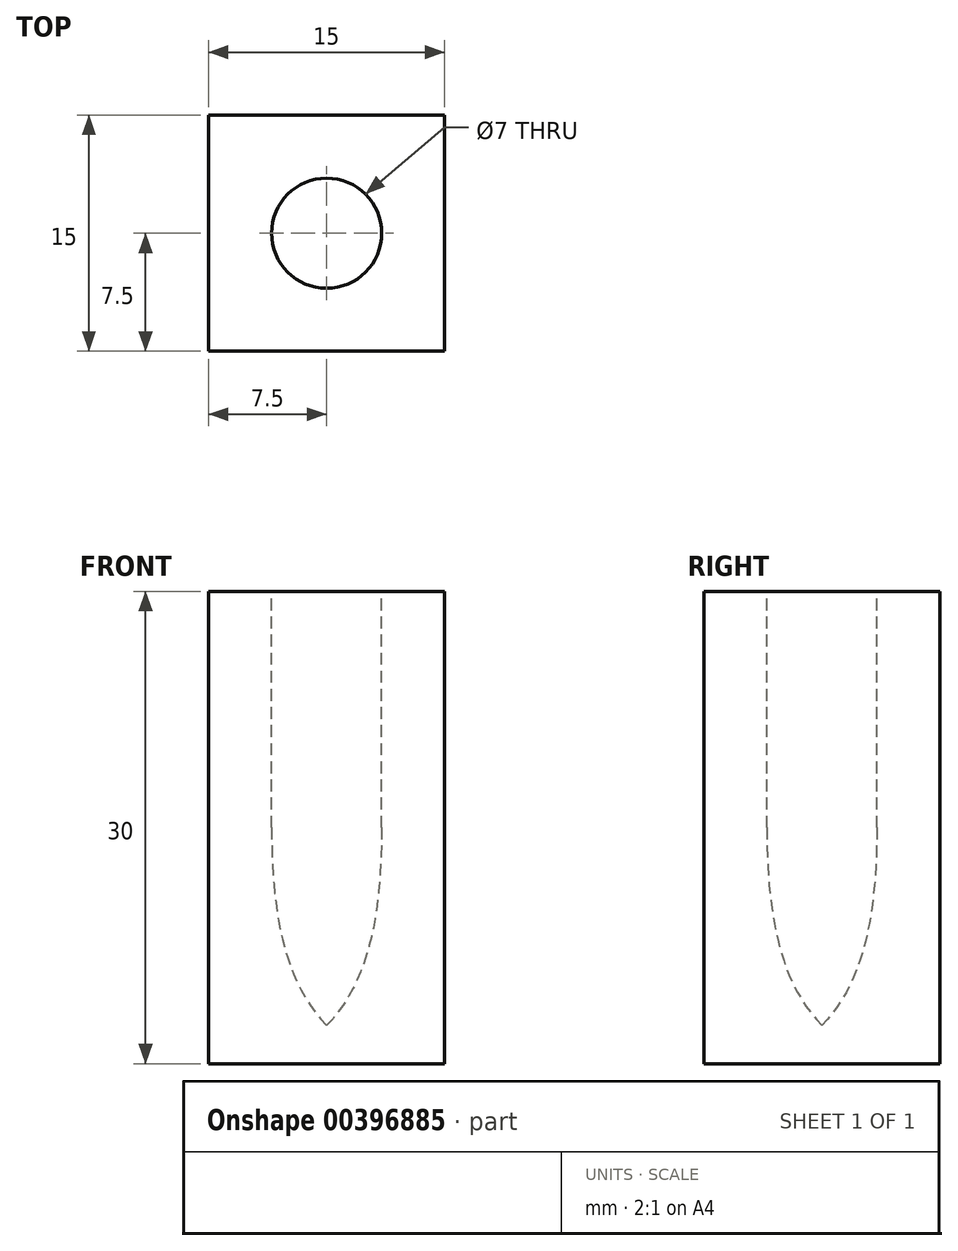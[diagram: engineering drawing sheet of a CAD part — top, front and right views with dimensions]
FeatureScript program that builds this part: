
annotation { "Feature Type Name" : "Feature", "Feature Type Description" : "" }
export const myFeature = defineFeature(function(context is Context, id is Id, definition is map)
    precondition{}
    {
        {
            var Q0;
            Q0=qCreatedBy(makeId("Top.planeOp"),FACE);
            var sketch = newSketch(context, id + "F0", { "sketchPlane" : qUnion([Q0])});
            skLineSegment(sketch, "E0.bottom", {"start": v(7.5, 7.5) * mm, "end": v(-7.5, 7.5) * mm});
            skLineSegment(sketch, "E0.top", {"start": v(7.5, -7.5) * mm, "end": v(-7.5, -7.5) * mm});
            skLineSegment(sketch, "E0.left", {"start": v(7.5, 7.5) * mm, "end": v(7.5, -7.5) * mm});
            skLineSegment(sketch, "E0.right", {"start": v(-7.5, 7.5) * mm, "end": v(-7.5, -7.5) * mm});
            skPoint(sketch, "E0.middle", {"position": v(0, 0) * mm});
            skSolve(sketch);
        }
        {
            var Q0;
            Q0 = qSketchRegion(id + "F0", true);
            extrude(context, id + "F1", {"entities" : qUnion([Q0]), "depth" : 30 * mm});
        }
        {
            var Q0;
            Q0=makeQuery(id+"F1.opExtrude","CAP_FACE",FACE,{"disambiguationData":[OSD([sQuery(id+"F0.wireOp",EDGE,"E0.bottom"),sQuery(id+"F0.wireOp",EDGE,"E0.top"),sQuery(id+"F0.wireOp",EDGE,"E0.left"),sQuery(id+"F0.wireOp",EDGE,"E0.right")])],"isStart":false});
            var sketch = newSketch(context, id + "F2", { "sketchPlane" : qUnion([Q0])});
            skCircle(sketch, "E1", {"center": v(0, 0) * mm, "radius": 3.5 * mm});
            skSolve(sketch);
        }
        {
            var Q0;
            Q0 = qSketchRegion(id + "F2", true);
            extrude(context, id + "F3", {"entities" : qUnion([Q0]), "operationType" : NewBodyOperationType.REMOVE, "oppositeDirection" : true, "depth" : 15 * mm});
        }
        {
            var Q0;
            Q0=qCreatedBy(makeId("Front.planeOp"),FACE);
            var sketch = newSketch(context, id + "F4", { "sketchPlane" : qUnion([Q0])});
            skLineSegment(sketch, "E2", {"start": v(0, 15.43) * mm, "end": v(0, 2.43) * mm});
            skLineSegment(sketch, "E3", {"start": v(-3.5, 15.17) * mm, "end": v(0, 15.43) * mm});
            skFitSpline(sketch, "E4", {"points": [v(-3.5, 15.17) * mm, v(0, 2.43) * mm], "startDerivative": vector(0.1, -13.62) * mm, "endDerivative": vector(9.22, -9.42) * mm});
            skSolve(sketch);
        }
        {
            var Q0;
            Q0 = qSketchRegion(id + "F4", true);
            var Q1;
            Q1=sQuery(id+"F4.wireOp",EDGE,"E2");
            var Q2;
            Q2=sQuery(id+"F4.wireOp",EDGE,"E2");
            revolve(context, id + "F5", {"operationType" : NewBodyOperationType.REMOVE, "entities" : qUnion([Q0]), "surfaceEntities" : qUnion([Q1]), "axis" : qUnion([Q2]), "revolveType" : RevolveType.FULL, "oppositeDirection" : true});
        }
    });
